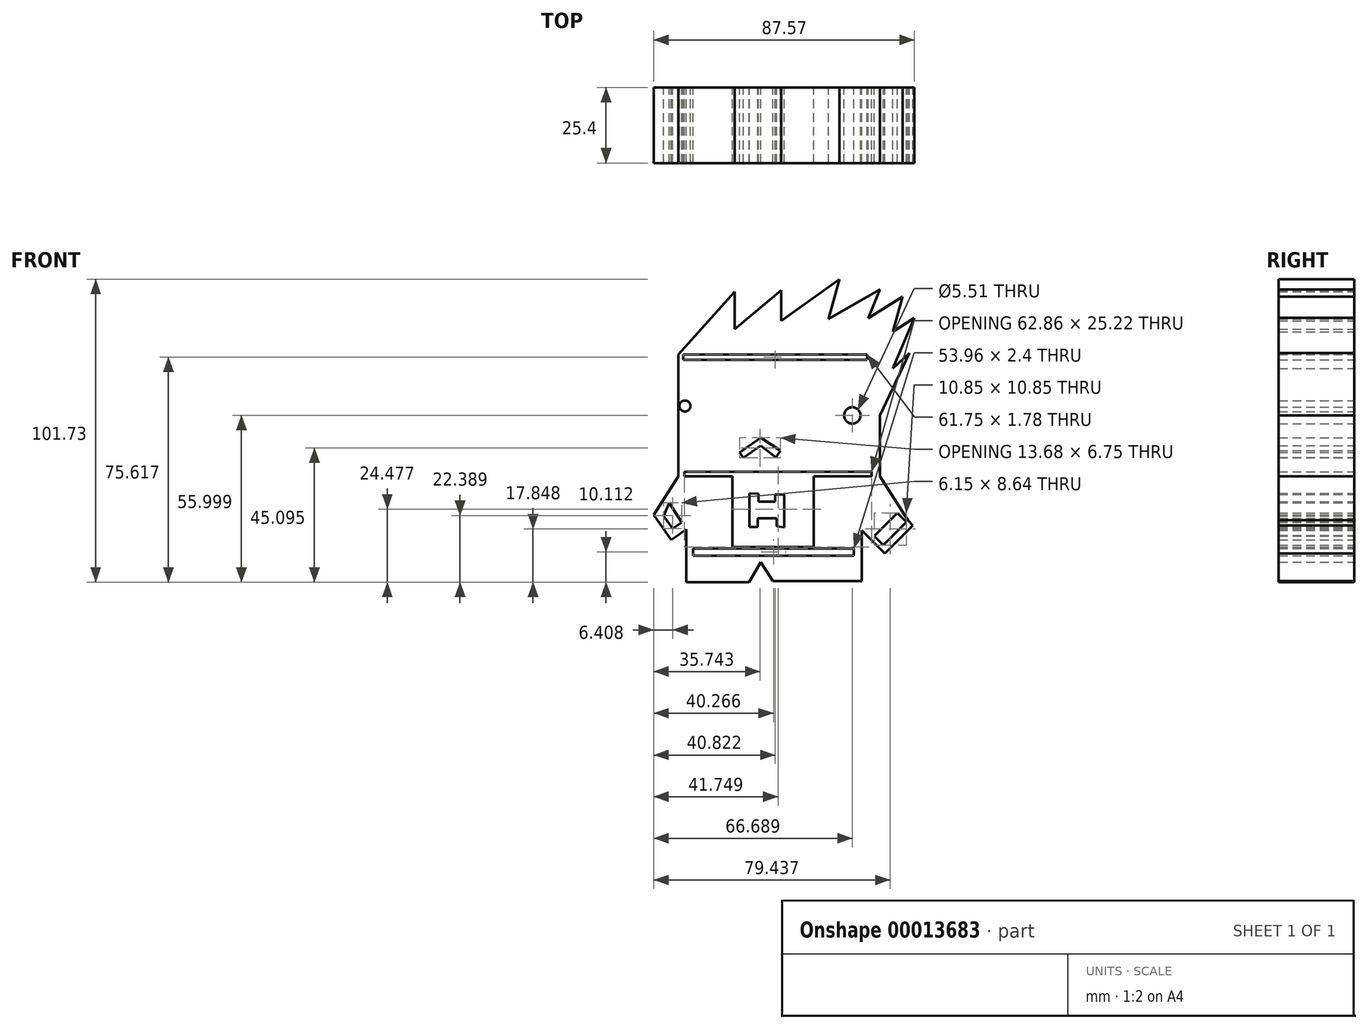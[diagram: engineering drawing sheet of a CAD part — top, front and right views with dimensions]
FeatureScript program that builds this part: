
annotation { "Feature Type Name" : "Feature", "Feature Type Description" : "" }
export const myFeature = defineFeature(function(context is Context, id is Id, definition is map)
    precondition{}
    {
        {
            var Q0;
            Q0=qCreatedBy(makeId("Front.planeOp"),FACE);
            var sketch = newSketch(context, id + "F0", { "sketchPlane" : qUnion([Q0])});
            skLineSegment(sketch, "E0.bottom", {"start": v(0, 0) * mm, "end": v(-67.66, 0) * mm});
            skLineSegment(sketch, "E0.top", {"start": v(0, 41) * mm, "end": v(-67.66, 41) * mm});
            skLineSegment(sketch, "E0.left", {"start": v(0, 0) * mm, "end": v(0, 41) * mm});
            skLineSegment(sketch, "E0.right", {"start": v(-67.66, 0) * mm, "end": v(-67.66, 41) * mm});
            skLineSegment(sketch, "E1", {"start": v(-67.66, 41) * mm, "end": v(-48.75, 62.04) * mm});
            skLineSegment(sketch, "E2", {"start": v(-48.75, 62.04) * mm, "end": v(-48.75, 49.44) * mm});
            skLineSegment(sketch, "E3", {"start": v(-48.75, 49.44) * mm, "end": v(-33.17, 62.56) * mm});
            skLineSegment(sketch, "E4", {"start": v(-33.17, 62.56) * mm, "end": v(-33.17, 51.76) * mm});
            skLineSegment(sketch, "E5", {"start": v(-33.83, 51.76) * mm, "end": v(-13.6, 66.22) * mm});
            skLineSegment(sketch, "E6", {"start": v(-13.6, 66.22) * mm, "end": v(-17.25, 52.9) * mm});
            skLineSegment(sketch, "E7", {"start": v(-17.25, 52.9) * mm, "end": v(0, 62.76) * mm});
            skLineSegment(sketch, "E8", {"start": v(0, 62.76) * mm, "end": v(-3.98, 53.08) * mm});
            skLineSegment(sketch, "E9", {"start": v(-3.98, 53.08) * mm, "end": v(7.63, 60.4) * mm});
            skLineSegment(sketch, "E10", {"start": v(7.63, 60.4) * mm, "end": v(4.31, 48.5) * mm});
            skLineSegment(sketch, "E11", {"start": v(4.31, 48.5) * mm, "end": v(11.6, 53.27) * mm});
            skLineSegment(sketch, "E12", {"start": v(11.6, 53.27) * mm, "end": v(4.31, 36.23) * mm});
            skLineSegment(sketch, "E13", {"start": v(4.31, 36.23) * mm, "end": v(9.95, 41.51) * mm});
            skLineSegment(sketch, "E14", {"start": v(9.95, 41.51) * mm, "end": v(0, 20.5) * mm});
            skLineSegment(sketch, "E15", {"start": v(-45.8, 6.21) * mm, "end": v(-40.05, 10.3) * mm});
            skLineSegment(sketch, "E16", {"start": v(-40.05, 10.3) * mm, "end": v(-34.86, 6.4) * mm});
            skLineSegment(sketch, "E17", {"start": v(-34.86, 6.4) * mm, "end": v(-40.05, 10.3) * mm});
            skCircle(sketch, "E18", {"center": v(-9.27, 20.49) * mm, "radius": 2.76 * mm});
            skCircle(sketch, "E19", {"center": v(-65.45, 23.64) * mm, "radius": 1.85 * mm});
            skLineSegment(sketch, "E20", {"start": v(-67.66, 0) * mm, "end": v(-74.54, -10.66) * mm});
            skLineSegment(sketch, "E21", {"start": v(-74.54, -10.66) * mm, "end": v(-67.86, -19.75) * mm});
            skLineSegment(sketch, "E22", {"start": v(-67.86, -19.75) * mm, "end": v(-65.06, -17.69) * mm});
            skLineSegment(sketch, "E23", {"start": v(-65.06, -17.69) * mm, "end": v(-65.06, -35.5) * mm});
            skLineSegment(sketch, "E24", {"start": v(-65.06, -35.5) * mm, "end": v(-43.95, -35.5) * mm});
            skLineSegment(sketch, "E25", {"start": v(-43.95, -35.5) * mm, "end": v(-40.05, -28.83) * mm});
            skLineSegment(sketch, "E26", {"start": v(-40.05, -28.83) * mm, "end": v(-35.97, -35.14) * mm});
            skLineSegment(sketch, "E27", {"start": v(-35.97, -35.14) * mm, "end": v(-6.12, -35.14) * mm});
            skLineSegment(sketch, "E28", {"start": v(-6.12, -35.14) * mm, "end": v(-6.12, -18.08) * mm});
            skLineSegment(sketch, "E29", {"start": v(-6.12, -18.08) * mm, "end": v(0, -24.2) * mm});
            skLineSegment(sketch, "E30", {"start": v(0, -24.2) * mm, "end": v(9.46, -14.74) * mm});
            skLineSegment(sketch, "E31", {"start": v(9.46, -14.74) * mm, "end": v(0, 0) * mm});
            skLineSegment(sketch, "E32", {"start": v(-65.06, -23.64) * mm, "end": v(-6.12, -23.64) * mm});
            skLineSegment(sketch, "E33", {"start": v(-6.12, -23.64) * mm, "end": v(-65.06, -23.64) * mm});
            skLineSegment(sketch, "E34", {"start": v(-49.5, 0) * mm, "end": v(-49.5, -23.64) * mm});
            skLineSegment(sketch, "E35", {"start": v(-49.5, -23.64) * mm, "end": v(-22.25, -23.64) * mm});
            skLineSegment(sketch, "E36", {"start": v(-22.25, -23.64) * mm, "end": v(-22.25, 0) * mm});
            skLineSegment(sketch, "E37", {"start": v(-22.25, 0) * mm, "end": v(-49.5, 0) * mm});
            skLineSegment(sketch, "E38", {"start": v(-43.76, -5.66) * mm, "end": v(-43.76, -16.97) * mm});
            skLineSegment(sketch, "E39", {"start": v(-43.76, -16.97) * mm, "end": v(-43.76, -5.66) * mm});
            skLineSegment(sketch, "E40", {"start": v(-43.76, -11.31) * mm, "end": v(-32.08, -11.31) * mm});
            skLineSegment(sketch, "E41", {"start": v(-32.08, -11.31) * mm, "end": v(-32.08, -6.03) * mm});
            skLineSegment(sketch, "E42", {"start": v(-32.08, -6.03) * mm, "end": v(-32.08, -17.15) * mm});
            skLineSegment(sketch, "E43", {"start": v(-32.08, -17.15) * mm, "end": v(-32.08, -6.03) * mm});
            skLineSegment(sketch, "E44", {"start": v(-72.03, -6.78) * mm, "end": v(-65.06, -17.69) * mm});
            skLineSegment(sketch, "E45", {"start": v(-3.06, -21.14) * mm, "end": v(7.07, -11.01) * mm});
            skLineSegment(sketch, "E46", {"start": v(-45.8, 6.21) * mm, "end": v(-47.06, 7.99) * mm});
            skLineSegment(sketch, "E47", {"start": v(-47.06, 7.99) * mm, "end": v(-40.05, 12.96) * mm});
            skLineSegment(sketch, "E48", {"start": v(-40.05, 12.96) * mm, "end": v(-33.38, 8.62) * mm});
            skLineSegment(sketch, "E49", {"start": v(-33.38, 8.62) * mm, "end": v(-34.86, 6.4) * mm});
            skLineSegment(sketch, "E50", {"start": v(-43.76, -16.97) * mm, "end": v(-40.98, -16.97) * mm});
            skLineSegment(sketch, "E51", {"start": v(-40.98, -16.97) * mm, "end": v(-40.98, -14) * mm});
            skLineSegment(sketch, "E52", {"start": v(-40.98, -14) * mm, "end": v(-34.67, -14) * mm});
            skLineSegment(sketch, "E53", {"start": v(-34.67, -14) * mm, "end": v(-34.67, -16.78) * mm});
            skLineSegment(sketch, "E54", {"start": v(-34.67, -16.78) * mm, "end": v(-32.08, -17.15) * mm});
            skLineSegment(sketch, "E55", {"start": v(-32.08, -6.03) * mm, "end": v(-35.23, -6.03) * mm});
            skLineSegment(sketch, "E56", {"start": v(-35.23, -6.03) * mm, "end": v(-35.23, -8.44) * mm});
            skLineSegment(sketch, "E57", {"start": v(-35.23, -8.44) * mm, "end": v(-40.8, -8.44) * mm});
            skLineSegment(sketch, "E58", {"start": v(-40.8, -8.44) * mm, "end": v(-40.8, -5.84) * mm});
            skLineSegment(sketch, "E59", {"start": v(-40.8, -5.84) * mm, "end": v(-43.76, -5.66) * mm});
            skLineSegment(sketch, "E60", {"start": v(-74.54, -10.66) * mm, "end": v(-75.96, -12.86) * mm});
            skLineSegment(sketch, "E61", {"start": v(-75.96, -12.86) * mm, "end": v(-70.09, -21.23) * mm});
            skLineSegment(sketch, "E62", {"start": v(-70.09, -21.23) * mm, "end": v(-67.86, -19.75) * mm});
            skLineSegment(sketch, "E63", {"start": v(0, -24.2) * mm, "end": v(1.67, -25.87) * mm});
            skLineSegment(sketch, "E64", {"start": v(1.67, -25.87) * mm, "end": v(11.03, -16.5) * mm});
            skLineSegment(sketch, "E65", {"start": v(11.03, -16.5) * mm, "end": v(9.46, -14.74) * mm});
            skLineSegment(sketch, "E66", {"start": v(-65.06, -24.2) * mm, "end": v(-6.12, -24.2) * mm});
            skLineSegment(sketch, "E67", {"start": v(-67.66, 39.22) * mm, "end": v(-1.67, 39.22) * mm});
            skLineSegment(sketch, "E68", {"start": v(-1.67, 39.22) * mm, "end": v(-1.67, 20.86) * mm});
            skLineSegment(sketch, "E69", {"start": v(-1.67, 20.86) * mm, "end": v(0.56, 20.3) * mm});
            skLineSegment(sketch, "E70", {"start": v(-67.66, 1.58) * mm, "end": v(0, 1.58) * mm});
            skLineSegment(sketch, "E71", {"start": v(-65.06, -26.6) * mm, "end": v(-6.12, -26.6) * mm});
            skLineSegment(sketch, "E72", {"start": v(5.84, -12.24) * mm, "end": v(8.9, -15.3) * mm});
            skLineSegment(sketch, "E73", {"start": v(-1.95, -20.03) * mm, "end": v(1.11, -23.09) * mm});
            skLineSegment(sketch, "E74", {"start": v(-72.63, -13.26) * mm, "end": v(-70.74, -8.8) * mm});
            skLineSegment(sketch, "E75", {"start": v(-69.56, -17.44) * mm, "end": v(-66.48, -15.47) * mm});
            skLineSegment(sketch, "E76", {"start": v(-62.67, -24.2) * mm, "end": v(-62.67, -26.6) * mm});
            skLineSegment(sketch, "E77", {"start": v(-8.71, -23.64) * mm, "end": v(-8.71, -26.6) * mm});
            skLineSegment(sketch, "E78", {"start": v(-65.64, 0) * mm, "end": v(-65.64, 1.58) * mm});
            skLineSegment(sketch, "E79", {"start": v(-2.78, 0) * mm, "end": v(-2.78, 1.58) * mm});
            skLineSegment(sketch, "E80", {"start": v(-66.01, 39.22) * mm, "end": v(-66.01, 41) * mm});
            skLineSegment(sketch, "E81", {"start": v(-4.26, 39.22) * mm, "end": v(-4.26, 41) * mm});
            skSolve(sketch);
        }
        {
            var Q0;
            Q0 = qSketchRegion(id + "F0", true);
            var Q1;
            {var subQ3=sQuery(id+"F0.wireOp",EDGE,"E40");Q1=makeQuery(id+"F0.imprint","IMPRINT",FACE,{"disambiguationData":[TD([[makeQuery(id+"F0.imprint","IMPRINT",EDGE,{"derivedFrom":subQ3}),1.0]])]});}
            var Q2;
            {var subQ3=sQuery(id+"F0.wireOp",EDGE,"E40");Q2=makeQuery(id+"F0.imprint","IMPRINT",FACE,{"disambiguationData":[TD([[makeQuery(id+"F0.imprint","IMPRINT",EDGE,{"derivedFrom":subQ3}),-1.0]])]});}
            extrude(context, id + "F1", {"entities" : qUnion([Q0, Q1, Q2]), "depth" : 25.4 * mm});
        }
    });
